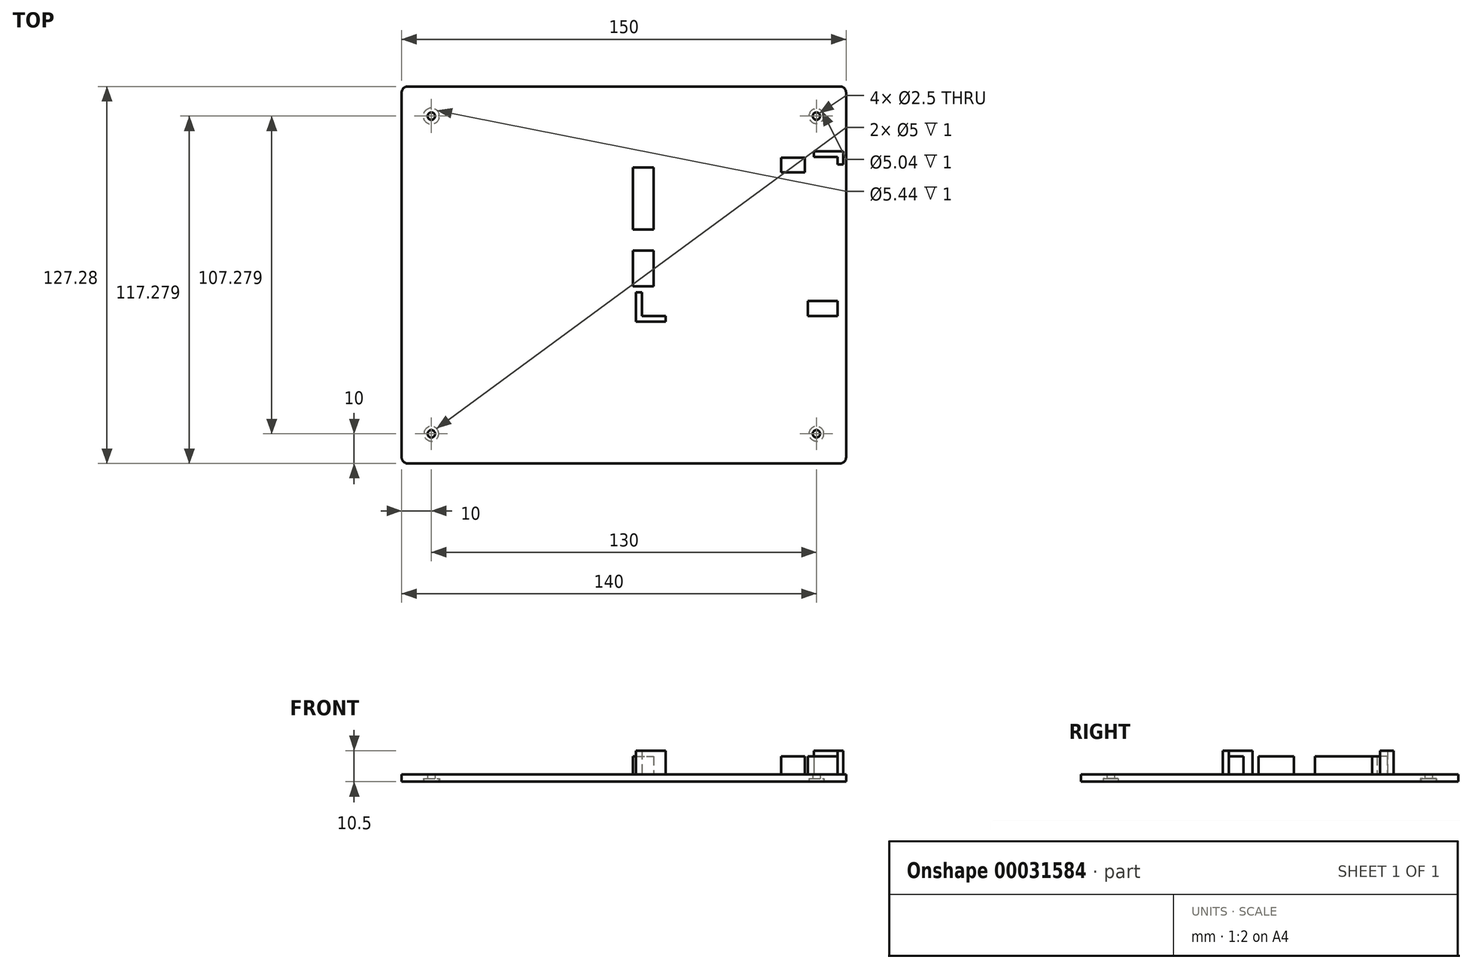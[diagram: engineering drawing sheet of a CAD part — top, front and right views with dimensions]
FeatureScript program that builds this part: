
annotation { "Feature Type Name" : "Feature", "Feature Type Description" : "" }
export const myFeature = defineFeature(function(context is Context, id is Id, definition is map)
    precondition{}
    {
        {
            var Q0;
            Q0=qCreatedBy(makeId("Top.planeOp"),FACE);
            var sketch = newSketch(context, id + "F0", { "sketchPlane" : qUnion([Q0])});
            skLineSegment(sketch, "E0", {"start": v(0, 0) * mm, "end": v(0, 127.28) * mm});
            skLineSegment(sketch, "E1", {"start": v(0, 0) * mm, "end": v(150, 0) * mm});
            skLineSegment(sketch, "E2", {"start": v(150, 0) * mm, "end": v(150, 127.28) * mm});
            skLineSegment(sketch, "E3", {"start": v(0, 127.28) * mm, "end": v(150, 127.28) * mm});
            skSolve(sketch);
        }
        {
            var Q0;
            Q0=makeQuery(id+"F0.imprint","IMPRINT",FACE,{"disambiguationData":[TD([[makeQuery(id+"F0.imprint","IMPRINT",EDGE,{"derivedFrom":sQuery(id+"F0.wireOp",EDGE,"E0")}),-1.0]])]});
            extrude(context, id + "F1", {"entities" : qUnion([Q0]), "depth" : 2.5 * mm});
        }
        {
            var Q0;
            Q0=makeQuery(id+"F1.opExtrude","CAP_FACE",FACE,{"disambiguationData":[OSD([sQuery(id+"F0.wireOp",EDGE,"E0"),sQuery(id+"F0.wireOp",EDGE,"E1"),sQuery(id+"F0.wireOp",EDGE,"E2"),sQuery(id+"F0.wireOp",EDGE,"E3")])],"isStart":true});
            var sketch = newSketch(context, id + "F2", { "sketchPlane" : qUnion([Q0])});
            skCircle(sketch, "E4", {"center": v(10, -10) * mm, "radius": 2.5 * mm});
            skCircle(sketch, "E5", {"center": v(140, -10) * mm, "radius": 2.5 * mm});
            skCircle(sketch, "E6", {"center": v(10, -117.28) * mm, "radius": 2.72 * mm});
            skCircle(sketch, "E7", {"center": v(140, -117.28) * mm, "radius": 2.52 * mm});
            skSolve(sketch);
        }
        {
            var Q0;
            Q0=qSketchRegion(id+"F2",true);
            extrude(context, id + "F3", {"entities" : qUnion([Q0]), "operationType" : NewBodyOperationType.REMOVE, "oppositeDirection" : true, "depth" : 1 * mm});
        }
        {
            var Q0;
            Q0=makeQuery(id+"F3.boolean.opBoolean","COPY",FACE,{"derivedFrom":makeQuery(id+"F3.opExtrude","CAP_FACE",FACE,{"disambiguationData":[OSD([sQuery(id+"F2.wireOp",EDGE,"E4")])],"isStart":false})});
            var sketch = newSketch(context, id + "F4", { "sketchPlane" : qUnion([Q0])});
            skCircle(sketch, "E8", {"center": v(10, -10) * mm, "radius": 1.25 * mm});
            skCircle(sketch, "E9", {"center": v(10, -117.28) * mm, "radius": 1.25 * mm});
            skCircle(sketch, "E10", {"center": v(140, -117.28) * mm, "radius": 1.25 * mm});
            skCircle(sketch, "E11", {"center": v(140, -10) * mm, "radius": 1.25 * mm});
            skSolve(sketch);
        }
        {
            var Q0;
            Q0=qSketchRegion(id+"F4",true);
            extrude(context, id + "F5", {"entities" : qUnion([Q0]), "operationType" : NewBodyOperationType.REMOVE, "endBound" : BoundingType.THROUGH_ALL, "oppositeDirection" : true, "depth" : 25 * mm});
        }
        {
            var Q0;
            Q0=makeQuery(id+"F1.opExtrude","SWEPT_EDGE",EDGE,{"disambiguationData":[OSD([sQuery(id+"F0.wireOp",EDGE,"E1"),sQuery(id+"F0.wireOp",EDGE,"E2")])]});
            var Q1;
            Q1=makeQuery(id+"F1.opExtrude","SWEPT_EDGE",EDGE,{"disambiguationData":[OSD([sQuery(id+"F0.wireOp",EDGE,"E0"),sQuery(id+"F0.wireOp",EDGE,"E1")])]});
            var Q2;
            Q2=makeQuery(id+"F1.opExtrude","SWEPT_EDGE",EDGE,{"disambiguationData":[OSD([sQuery(id+"F0.wireOp",EDGE,"E2"),sQuery(id+"F0.wireOp",EDGE,"E3")])]});
            var Q3;
            Q3=makeQuery(id+"F1.opExtrude","SWEPT_EDGE",EDGE,{"disambiguationData":[OSD([sQuery(id+"F0.wireOp",EDGE,"E0"),sQuery(id+"F0.wireOp",EDGE,"E3")])]});
            fillet(context, id + "F6", {"entities" : qUnion([Q0, Q1, Q2, Q3]), "radius" : 2 * mm, "tangentPropagation" : true, "allowEdgeOverflow" : false});
        }
        {
            var Q0;
            Q0=makeQuery(id+"F1.opExtrude","CAP_FACE",FACE,{"disambiguationData":[OSD([sQuery(id+"F0.wireOp",EDGE,"E0"),sQuery(id+"F0.wireOp",EDGE,"E1"),sQuery(id+"F0.wireOp",EDGE,"E2"),sQuery(id+"F0.wireOp",EDGE,"E3")])],"isStart":false});
            var sketch = newSketch(context, id + "F7", { "sketchPlane" : qUnion([Q0])});
            skLineSegment(sketch, "E12.bottom", {"start": v(81.05, 103.45) * mm, "end": v(89.05, 103.45) * mm, "construction": true});
            skLineSegment(sketch, "E12.top", {"start": v(81.05, 49.83) * mm, "end": v(89.05, 49.83) * mm});
            skLineSegment(sketch, "E12.left", {"start": v(81.05, 103.45) * mm, "end": v(81.05, 101.45) * mm});
            skLineSegment(sketch, "E12.right", {"start": v(147.1, 103.45) * mm, "end": v(147.1, 100.95) * mm});
            skLineSegment(sketch, "E13.0", {"start": v(79.05, 105.45) * mm, "end": v(89.05, 105.45) * mm, "construction": true});
            skLineSegment(sketch, "E13.1", {"start": v(79.05, 105.45) * mm, "end": v(79.05, 101.45) * mm, "construction": true});
            skLineSegment(sketch, "E13.2", {"start": v(79.05, 47.83) * mm, "end": v(89.05, 47.83) * mm});
            skLineSegment(sketch, "E13.3", {"start": v(149.1, 105.45) * mm, "end": v(149.1, 100.95) * mm});
            skLineSegment(sketch, "E14", {"start": v(139.1, 105.45) * mm, "end": v(139.1, 103.45) * mm});
            skLineSegment(sketch, "E15", {"start": v(79.05, 57.83) * mm, "end": v(81.05, 57.83) * mm});
            skLineSegment(sketch, "E16.trimOffspring", {"start": v(139.1, 47.83) * mm, "end": v(149.1, 47.83) * mm, "construction": true});
            skLineSegment(sketch, "E17.trimOffspring", {"start": v(139.1, 49.83) * mm, "end": v(147.1, 49.83) * mm, "construction": true});
            skLineSegment(sketch, "E18.trimOffspring", {"start": v(139.1, 103.45) * mm, "end": v(147.1, 103.45) * mm});
            skLineSegment(sketch, "E19.trimOffspring", {"start": v(139.1, 105.45) * mm, "end": v(149.1, 105.45) * mm});
            skLineSegment(sketch, "E20.trimOffspring", {"start": v(81.05, 57.83) * mm, "end": v(81.05, 49.83) * mm});
            skLineSegment(sketch, "E21.trimOffspring", {"start": v(79.05, 57.83) * mm, "end": v(79.05, 47.83) * mm});
            skLineSegment(sketch, "E22.trimOffspring", {"start": v(147.1, 57.83) * mm, "end": v(147.1, 49.83) * mm, "construction": true});
            skLineSegment(sketch, "E23.trimOffspring", {"start": v(149.1, 57.83) * mm, "end": v(149.1, 47.83) * mm, "construction": true});
            skLineSegment(sketch, "E24.trimOffspring", {"start": v(139.1, 49.83) * mm, "end": v(139.1, 38.04) * mm, "construction": true});
            skLineSegment(sketch, "E25.trimOffspring", {"start": v(147.1, 57.83) * mm, "end": v(149.1, 57.83) * mm, "construction": true});
            skLineSegment(sketch, "E26.trimOffspring", {"start": v(89.05, 49.83) * mm, "end": v(89.05, 47.83) * mm});
            skLineSegment(sketch, "E27", {"start": v(89.05, 105.45) * mm, "end": v(89.05, 103.45) * mm, "construction": true});
            skLineSegment(sketch, "E28", {"start": v(81.05, 101.45) * mm, "end": v(79.05, 101.45) * mm, "construction": true});
            skLineSegment(sketch, "E29", {"start": v(147.1, 100.95) * mm, "end": v(149.1, 100.95) * mm});
            skSolve(sketch);
        }
        {
            var Q0;
            Q0 = qSketchRegion(id + "F7", true);
            extrude(context, id + "F8", {"entities" : qUnion([Q0]), "operationType" : NewBodyOperationType.ADD, "depth" : 8 * mm});
        }
        {
            var Q0;
            Q0=makeQuery(id+"F1.opExtrude","CAP_FACE",FACE,{"disambiguationData":[OSD([sQuery(id+"F0.wireOp",EDGE,"E0"),sQuery(id+"F0.wireOp",EDGE,"E1"),sQuery(id+"F0.wireOp",EDGE,"E2"),sQuery(id+"F0.wireOp",EDGE,"E3")])],"isStart":false});
            var sketch = newSketch(context, id + "F9", { "sketchPlane" : qUnion([Q0])});
            skLineSegment(sketch, "E30.top", {"start": v(78.05, 59.83) * mm, "end": v(85.05, 59.83) * mm});
            skLineSegment(sketch, "E30.left", {"start": v(78.05, 99.95) * mm, "end": v(78.05, 78.95) * mm});
            skLineSegment(sketch, "E30.right", {"start": v(85.05, 99.95) * mm, "end": v(85.05, 78.95) * mm});
            skLineSegment(sketch, "E31", {"start": v(78.05, 99.95) * mm, "end": v(85.05, 99.95) * mm});
            skLineSegment(sketch, "E32.bottom", {"start": v(128.04, 103.28) * mm, "end": v(136.04, 103.28) * mm});
            skLineSegment(sketch, "E32.top", {"start": v(128.04, 98.28) * mm, "end": v(136.04, 98.28) * mm});
            skLineSegment(sketch, "E32.left", {"start": v(128.04, 103.28) * mm, "end": v(128.04, 98.28) * mm});
            skLineSegment(sketch, "E32.right", {"start": v(136.04, 103.28) * mm, "end": v(136.04, 98.28) * mm});
            skLineSegment(sketch, "E33", {"start": v(78.05, 71.83) * mm, "end": v(85.05, 71.83) * mm});
            skLineSegment(sketch, "E34", {"start": v(78.05, 78.95) * mm, "end": v(85.05, 78.95) * mm});
            skLineSegment(sketch, "E35.trimOffspring", {"start": v(85.05, 71.83) * mm, "end": v(85.05, 59.83) * mm});
            skLineSegment(sketch, "E36.trimOffspring", {"start": v(78.05, 71.83) * mm, "end": v(78.05, 59.83) * mm});
            skSolve(sketch);
        }
        {
            var Q0;
            Q0 = qSketchRegion(id + "F9", true);
            var Q1;
            Q1=sQuery(id+"F9.wireOp",EDGE,"E30.left");
            extrude(context, id + "F10", {"entities" : qUnion([Q0]), "operationType" : NewBodyOperationType.ADD, "surfaceEntities" : qUnion([Q1]), "depth" : 6 * mm});
        }
        {
            var Q0;
            Q0=makeQuery(id+"F1.opExtrude","CAP_FACE",FACE,{"disambiguationData":[OSD([sQuery(id+"F0.wireOp",EDGE,"E0"),sQuery(id+"F0.wireOp",EDGE,"E1"),sQuery(id+"F0.wireOp",EDGE,"E2"),sQuery(id+"F0.wireOp",EDGE,"E3")])],"isStart":false});
            var sketch = newSketch(context, id + "F11", { "sketchPlane" : qUnion([Q0])});
            skLineSegment(sketch, "E37.bottom", {"start": v(147.1, 49.83) * mm, "end": v(137.1, 49.83) * mm});
            skLineSegment(sketch, "E37.top", {"start": v(147.1, 54.83) * mm, "end": v(137.1, 54.83) * mm});
            skLineSegment(sketch, "E37.left", {"start": v(147.1, 49.83) * mm, "end": v(147.1, 54.83) * mm});
            skLineSegment(sketch, "E37.right", {"start": v(137.1, 49.83) * mm, "end": v(137.1, 54.83) * mm});
            skLineSegment(sketch, "E38.bottom", {"start": v(137.1, 49.83) * mm, "end": v(147.1, 49.83) * mm});
            skLineSegment(sketch, "E38.top", {"start": v(137.1, 54.83) * mm, "end": v(147.1, 54.83) * mm});
            skSolve(sketch);
        }
        {
            var Q0;
            Q0 = qSketchRegion(id + "F11", true);
            extrude(context, id + "F12", {"entities" : qUnion([Q0]), "operationType" : NewBodyOperationType.ADD, "depth" : 6 * mm});
        }
    });
